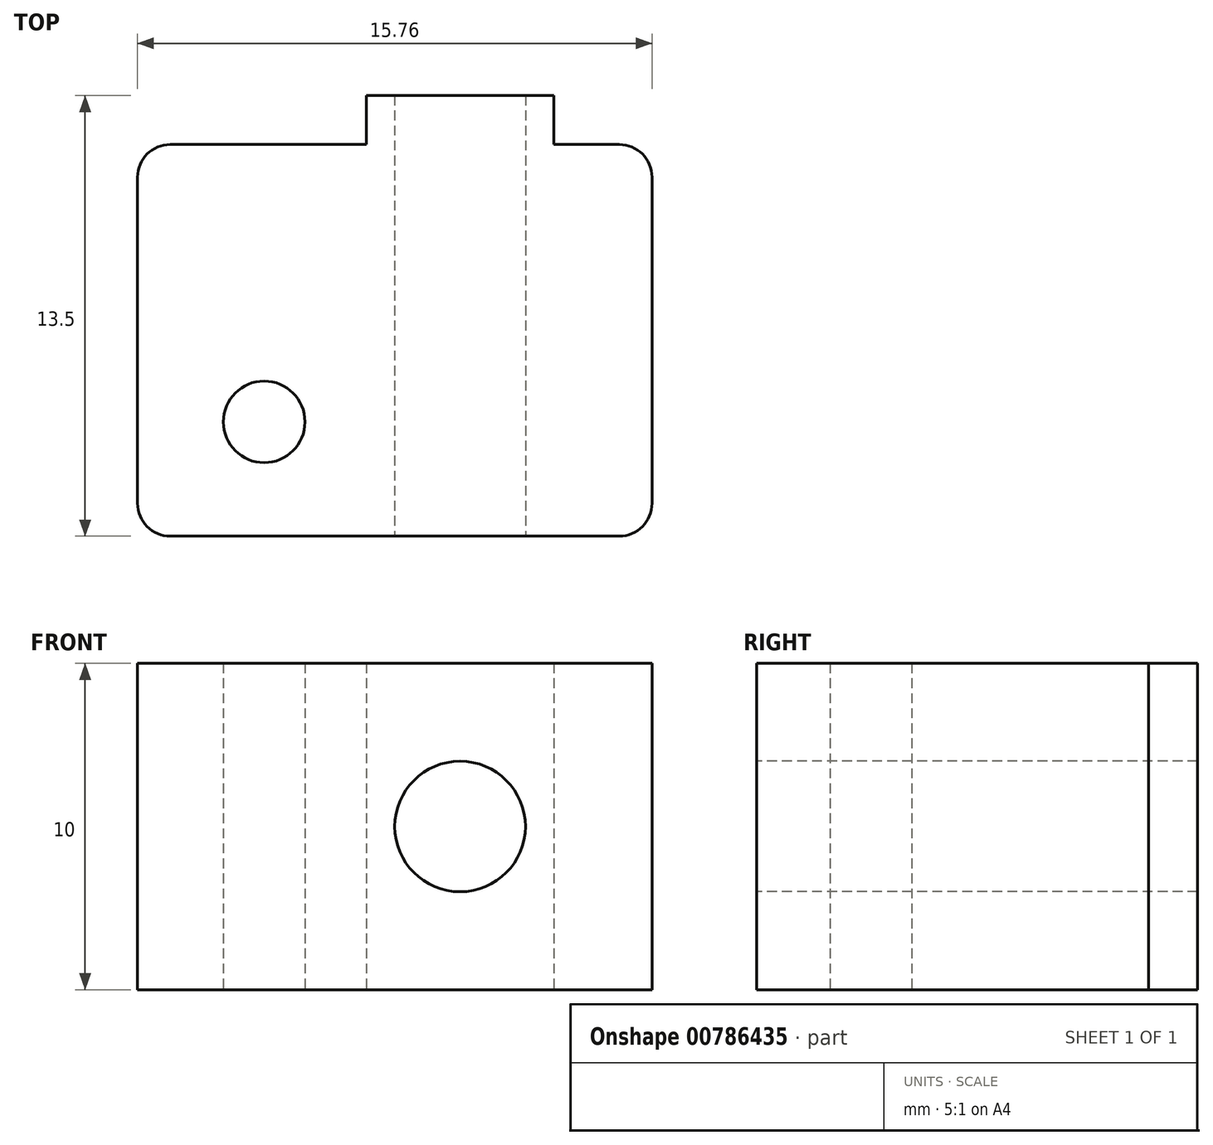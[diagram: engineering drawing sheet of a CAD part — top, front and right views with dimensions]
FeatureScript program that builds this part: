
annotation { "Feature Type Name" : "Feature", "Feature Type Description" : "" }
export const myFeature = defineFeature(function(context is Context, id is Id, definition is map)
    precondition{}
    {
        {
            var Q0;
            Q0=qCreatedBy(makeId("Top.planeOp"),FACE);
            var sketch = newSketch(context, id + "F0", { "sketchPlane" : qUnion([Q0])});
            skLineSegment(sketch, "E0", {"start": v(-2.88, 0) * mm, "end": v(-2.87, -1.5) * mm});
            skLineSegment(sketch, "E1", {"start": v(-2.87, -1.5) * mm, "end": v(-9.87, -1.5) * mm});
            skLineSegment(sketch, "E2", {"start": v(-9.87, -1.5) * mm, "end": v(-9.87, -13.5) * mm});
            skLineSegment(sketch, "E3", {"start": v(-9.87, -13.5) * mm, "end": v(5.88, -13.5) * mm});
            skLineSegment(sketch, "E4", {"start": v(5.88, -13.5) * mm, "end": v(5.88, -1.5) * mm});
            skLineSegment(sketch, "E5", {"start": v(5.88, -1.5) * mm, "end": v(2.87, -1.5) * mm});
            skLineSegment(sketch, "E6", {"start": v(2.88, -1.5) * mm, "end": v(2.88, 0) * mm});
            skLineSegment(sketch, "E7", {"start": v(2.87, 0) * mm, "end": v(-2.88, 0) * mm});
            skCircle(sketch, "E8", {"center": v(-6, -10) * mm, "radius": 1.25 * mm});
            skLineSegment(sketch, "E9", {"start": v(0, 1.6) * mm, "end": v(0, -15.35) * mm, "construction": true});
            skSolve(sketch);
        }
        {
            var Q0;
            Q0 = qSketchRegion(id + "F0", true);
            extrude(context, id + "F1", {"entities" : qUnion([Q0]), "depth" : 10 * mm, "offsetDistance" : 25 * mm});
        }
        {
            var Q0;
            Q0=makeQuery(id+"F1.opExtrude","SWEPT_FACE",FACE,{"disambiguationData":[OSD([sQuery(id+"F0.wireOp",EDGE,"E3")])]});
            var sketch = newSketch(context, id + "F2", { "sketchPlane" : qUnion([Q0])});
            skLineSegment(sketch, "E10", {"start": v(0, -1.09) * mm, "end": v(0, 11.09) * mm, "construction": true});
            skLineSegment(sketch, "E11", {"start": v(-149.32, 5) * mm, "end": v(-162.54, 5) * mm, "construction": true});
            skPoint(sketch, "E11.startSnap0", {"position": v(5.87, 5) * mm});
            skCircle(sketch, "E12", {"center": v(0, 5) * mm, "radius": 2 * mm});
            skSolve(sketch);
        }
        {
            var Q0;
            Q0 = qSketchRegion(id + "F2", true);
            var Q1;
            Q1 = qConstructionFilter(qBodyType(qCreatedBy(id + "F2" ,EDGE), BodyType.WIRE), ConstructionObject.NO);
            extrude(context, id + "F3", {"entities" : qUnion([Q0]), "operationType" : NewBodyOperationType.REMOVE, "surfaceEntities" : qUnion([Q1]), "endBound" : BoundingType.THROUGH_ALL, "oppositeDirection" : true, "depth" : 25 * mm, "offsetDistance" : 25 * mm});
        }
        {
            var Q0;
            Q0=makeQuery(id+"F1.opExtrude","SWEPT_EDGE",EDGE,{"disambiguationData":[OSD([sQuery(id+"F0.wireOp",EDGE,"E4"),sQuery(id+"F0.wireOp",EDGE,"E5")])]});
            var Q1;
            Q1=makeQuery(id+"F1.opExtrude","SWEPT_EDGE",EDGE,{"disambiguationData":[OSD([sQuery(id+"F0.wireOp",EDGE,"E3"),sQuery(id+"F0.wireOp",EDGE,"E4")])]});
            var Q2;
            Q2=makeQuery(id+"F1.opExtrude","SWEPT_EDGE",EDGE,{"disambiguationData":[OSD([sQuery(id+"F0.wireOp",EDGE,"E3"),sQuery(id+"F0.wireOp",EDGE,"CpxsBWRZ-9mAr-sJV6-9N8Q-FtQSNL9tesOz")])]});
            var Q3;
            Q3=makeQuery(id+"F1.opExtrude","SWEPT_EDGE",EDGE,{"disambiguationData":[OSD([sQuery(id+"F0.wireOp",EDGE,"iWGhxFLs-JUY7-LwzM-lr5B-QrbU4ywkjIja"),sQuery(id+"F0.wireOp",EDGE,"CpxsBWRZ-9mAr-sJV6-9N8Q-FtQSNL9tesOz")])]});
            var Q4;
            Q4=makeQuery(id+"F1.opExtrude","SWEPT_EDGE",EDGE,{"disambiguationData":[OSD([sQuery(id+"F0.wireOp",EDGE,"E1"),sQuery(id+"F0.wireOp",EDGE,"E2")])]});
            fillet(context, id + "F4", {"entities" : qUnion([Q0, Q1, Q2, Q3, Q4]), "radius" : 1 * mm, "tangentPropagation" : true, "allowEdgeOverflow" : false});
        }
    });
